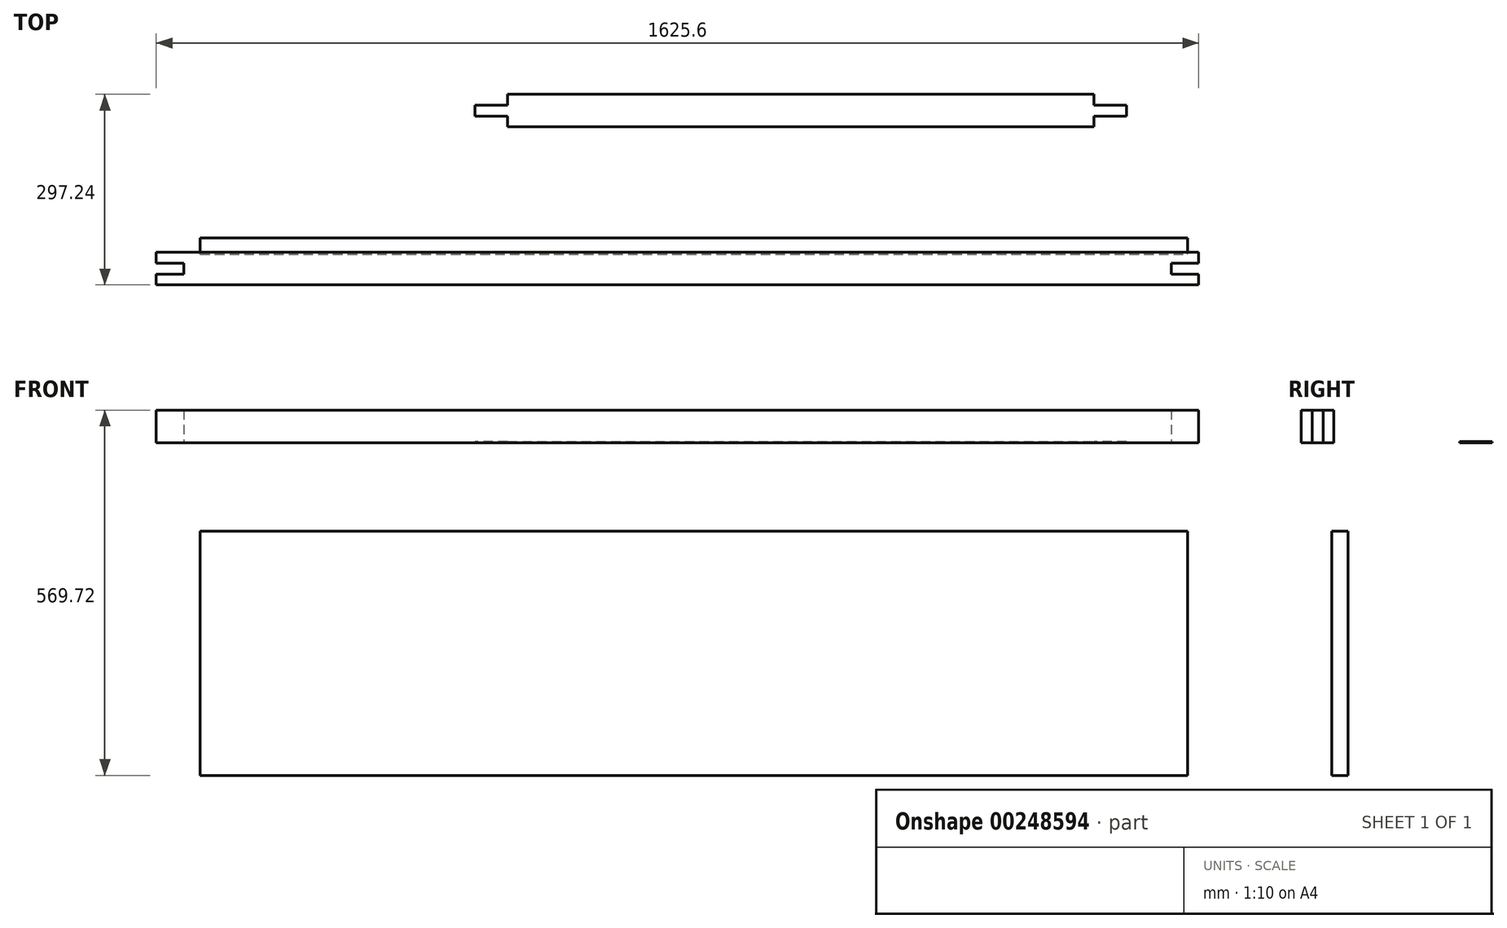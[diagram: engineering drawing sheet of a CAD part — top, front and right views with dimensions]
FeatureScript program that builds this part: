
annotation { "Feature Type Name" : "Feature", "Feature Type Description" : "" }
export const myFeature = defineFeature(function(context is Context, id is Id, definition is map)
    precondition{}
    {
        {
            var Q0;
            Q0=qCreatedBy(makeId("Top.planeOp"),FACE);
            var sketch = newSketch(context, id + "F0", { "sketchPlane" : qUnion([Q0])});
            skLineSegment(sketch, "E0", {"start": v(-811.94, -39.2) * mm, "end": v(-811.94, -22.26) * mm});
            skLineSegment(sketch, "E1", {"start": v(-811.94, -22.26) * mm, "end": v(813.66, -22.26) * mm});
            skLineSegment(sketch, "E2", {"start": v(813.66, -22.26) * mm, "end": v(813.66, -39.2) * mm});
            skLineSegment(sketch, "E3", {"start": v(813.66, -39.2) * mm, "end": v(770.8, -39.2) * mm});
            skLineSegment(sketch, "E4", {"start": v(770.8, -39.2) * mm, "end": v(770.8, -56.13) * mm});
            skLineSegment(sketch, "E5", {"start": v(770.8, -56.13) * mm, "end": v(813.66, -56.13) * mm});
            skLineSegment(sketch, "E6", {"start": v(813.66, -56.13) * mm, "end": v(813.66, -73.06) * mm});
            skLineSegment(sketch, "E7", {"start": v(813.66, -73.06) * mm, "end": v(-811.94, -73.06) * mm});
            skLineSegment(sketch, "E8", {"start": v(-811.94, -73.06) * mm, "end": v(-811.94, -56.13) * mm});
            skLineSegment(sketch, "E9", {"start": v(-811.94, -56.13) * mm, "end": v(-769.08, -56.13) * mm});
            skLineSegment(sketch, "E10", {"start": v(-769.08, -56.13) * mm, "end": v(-769.08, -39.2) * mm});
            skLineSegment(sketch, "E11", {"start": v(-769.08, -39.2) * mm, "end": v(-811.94, -39.2) * mm});
            skSolve(sketch);
        }
        {
            var Q0;
            Q0=makeQuery(id+"F0.imprint","IMPRINT",FACE,{"disambiguationData":[TD([[makeQuery(id+"F0.imprint","IMPRINT",EDGE,{"derivedFrom":sQuery(id+"F0.wireOp",EDGE,"E0")}),-1.0]])]});
            extrude(context, id + "F1", {"entities" : qUnion([Q0]), "depth" : 50.8 * mm});
        }
        {
            var Q0;
            Q0=qCreatedBy(makeId("Front.planeOp"),FACE);
            var sketch = newSketch(context, id + "F2", { "sketchPlane" : qUnion([Q0])});
            skLineSegment(sketch, "E12.bottom", {"start": v(-743.52, -137.92) * mm, "end": v(796.35, -137.92) * mm});
            skLineSegment(sketch, "E12.top", {"start": v(-743.52, -518.92) * mm, "end": v(796.35, -518.92) * mm});
            skLineSegment(sketch, "E12.left", {"start": v(-743.52, -137.92) * mm, "end": v(-743.52, -518.92) * mm});
            skLineSegment(sketch, "E12.right", {"start": v(796.35, -137.92) * mm, "end": v(796.35, -518.92) * mm});
            skSolve(sketch);
        }
        {
            var Q0;
            Q0=qSketchRegion(id+"F2",true);
            extrude(context, id + "F3", {"entities" : qUnion([Q0]), "depth" : 25.4 * mm});
        }
        {
            var Q0;
            Q0=qCreatedBy(makeId("Top.planeOp"),FACE);
            var sketch = newSketch(context, id + "F4", { "sketchPlane" : qUnion([Q0])});
            skLineSegment(sketch, "E13", {"start": v(-264, 224.18) * mm, "end": v(650.4, 224.18) * mm});
            skLineSegment(sketch, "E14", {"start": v(650.4, 207.25) * mm, "end": v(701.2, 207.25) * mm});
            skLineSegment(sketch, "E15", {"start": v(701.2, 207.25) * mm, "end": v(701.2, 190.32) * mm});
            skLineSegment(sketch, "E16", {"start": v(701.2, 190.32) * mm, "end": v(650.4, 190.32) * mm});
            skLineSegment(sketch, "E17", {"start": v(650.4, 190.32) * mm, "end": v(650.4, 173.38) * mm});
            skLineSegment(sketch, "E18", {"start": v(650.4, 173.38) * mm, "end": v(-264, 173.38) * mm});
            skLineSegment(sketch, "E19", {"start": v(650.4, 224.18) * mm, "end": v(650.4, 207.25) * mm});
            skLineSegment(sketch, "E20", {"start": v(-264, 224.18) * mm, "end": v(-264, 207.25) * mm});
            skLineSegment(sketch, "E21", {"start": v(-264, 207.25) * mm, "end": v(-314.8, 207.25) * mm});
            skLineSegment(sketch, "E22", {"start": v(-314.8, 207.25) * mm, "end": v(-314.8, 190.32) * mm});
            skLineSegment(sketch, "E23", {"start": v(-314.8, 190.32) * mm, "end": v(-264, 190.32) * mm});
            skLineSegment(sketch, "E24", {"start": v(-264, 190.32) * mm, "end": v(-264, 173.38) * mm});
            skSolve(sketch);
        }
        {
            var Q0;
            Q0=makeQuery(id+"F4.imprint","IMPRINT",FACE,{"disambiguationData":[TD([[makeQuery(id+"F4.imprint","IMPRINT",EDGE,{"derivedFrom":sQuery(id+"F4.wireOp",EDGE,"E13")}),-1.0]])]});
            extrude(context, id + "F5", {"entities" : qUnion([Q0]), "depth" : (1 + (11 / 16)) * mm});
        }
    });
